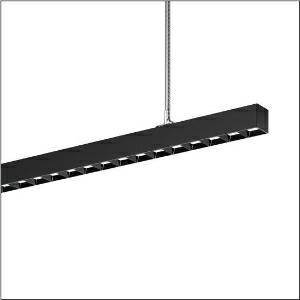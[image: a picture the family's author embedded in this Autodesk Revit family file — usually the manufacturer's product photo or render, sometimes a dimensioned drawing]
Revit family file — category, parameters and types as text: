
# Revit family: silica_r__21_51mx31dc4dbb_76cd
name_source: partatom
category: Lighting Fixtures
units: mm (PartAtom-declared; Revit-internal decimal feet)

## family parameters
Cut with Voids When Loaded = No
Host = Face
Light Source = No
Part Type = Normal
Room Calculation Point = No
Round Connector Dimension = Use Diameter
Shared = No

## types (1)
- --- (1 x LED, 18230 lm, 105.9 W, 4000K)
    Apparent Load = 106 VA
    CIE Flux Codes = 87 99 100 59 100
    Color Rendering = 80
    Color Temperature = 4000K
    Default Elevation = 1800 mm
    Description = Silica® 21, office luminaire, primary light control with darklight reflector, of PMMA, black, CAT 2 (L<= 3000cd/m²), light emission: direct/indirect distribution, primary light characteristic: symmetric, installation type: suspended mounting, LED, rated luminous flux: 18.230lm, luminous efficacy: 172lm/W, light colour: 840, colour temperature: 4000K, control gear: DALI 2, with terminal, 3+2-pole, max. 2.5mm², mains connection: 220..240V, AC, 50/60Hz, rated input power: 105.9W, luminaire housing, of aluminium, matt jet black (RAL 9005), length: 3.004mm, width: 53mm, height: 53mm, protection rating (complete): IP20, insulation class (complete): insulation class I (protective earthing), certification: CE, permissible operating ambient temperature: 0..+35°C, standard: EN 50419, packaging unit: 1 piece
    Height = 53 mm
    Lamp = 1 x LED
    Lamp Light Flux = 18230 lm
    Lamp Power = 105.9 W
    Lamp count = 1
    Length = 3004 mm
    Luminous efficacy = 172 lm/W
    Manufacturer = Siteco
    ModVariant = No
    Model = 51MX31DC4DBB
    Mounting Place = Ceiling
    Mounting Type = Pendant
    Number of Poles = 1
    OnlyDefault = Yes
    Power Factor = 1
    Product Name = Silica® 21
    Product group = office luminaire | ceiling pendant
    ProductGroupID = 904
    Protection Class = Protection class I
    Protection Degree = IP 20
    RLX_Detail_Level = 1
    RLX_Emergency_Light_Flux = 0 lm
    RLX_Emergency_Type = 0
    RLX_Emergency_Type_DB = No
    RlxData = <blob elided: 67289 chars, md5=0249d643>
    Socket = socket
    Standby Power = 0 W
    System Light Flux = 18230 lm
    System Power = 106 W
    Type Comments = factory setting: luminous flux: 100 % | dim-lin: 254 | 367 mA
    Type Image = l_1335852.jpg
    URL = http://relux.com
    VarID = @adj_121102
    Voltage = 0 V
    Weight = 0.00 kg
    Width = 53 mm

## geometry (parser evidence)
native form markers: Blend x4, Sweep x12
no freeform markers — native parametric forms only
